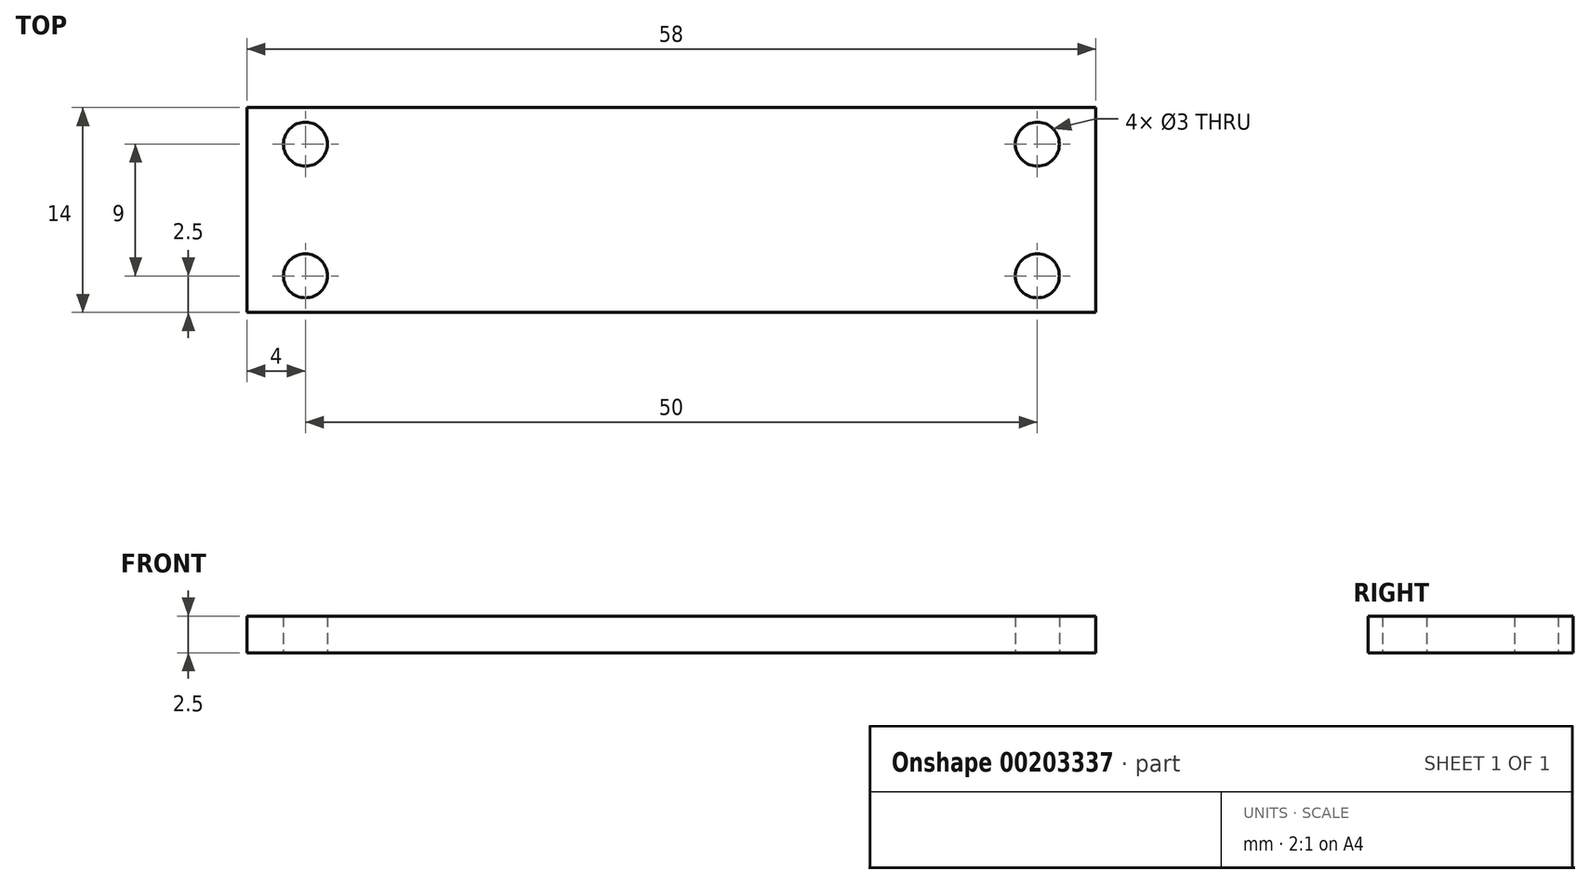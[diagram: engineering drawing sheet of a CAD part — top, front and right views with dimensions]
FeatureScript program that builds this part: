
annotation { "Feature Type Name" : "Feature", "Feature Type Description" : "" }
export const myFeature = defineFeature(function(context is Context, id is Id, definition is map)
    precondition{}
    {
        {
            var Q0;
            Q0=qCreatedBy(makeId("Top.planeOp"),FACE);
            var sketch = newSketch(context, id + "F0", { "sketchPlane" : qUnion([Q0])});
            skLineSegment(sketch, "E0.bottom", {"start": v(-29, 14) * mm, "end": v(29, 14) * mm});
            skLineSegment(sketch, "E0.top", {"start": v(-29, 9) * mm, "end": v(29, 9) * mm});
            skLineSegment(sketch, "E0.left", {"start": v(-29, 14) * mm, "end": v(-29, 9) * mm});
            skLineSegment(sketch, "E0.right", {"start": v(29, 14) * mm, "end": v(29, 9) * mm});
            skLineSegment(sketch, "E1", {"start": v(-29, 11.5) * mm, "end": v(29, 11.5) * mm, "construction": true});
            skCircle(sketch, "E2", {"center": v(-25, 11.5) * mm, "radius": 1.5 * mm});
            skCircle(sketch, "E3", {"center": v(25, 11.5) * mm, "radius": 1.5 * mm});
            skLineSegment(sketch, "E4", {"start": v(0, 14) * mm, "end": v(0, 9) * mm, "construction": true});
            skLineSegment(sketch, "E5.top", {"start": v(-29, 0) * mm, "end": v(29, 0) * mm});
            skLineSegment(sketch, "E5.left", {"start": v(-29, 9) * mm, "end": v(-29, 0) * mm});
            skLineSegment(sketch, "E5.right", {"start": v(29, 9) * mm, "end": v(29, 0) * mm});
            skLineSegment(sketch, "E6", {"start": v(-29, 5) * mm, "end": v(29, 5) * mm, "construction": true});
            skLineSegment(sketch, "E7", {"start": v(-29, 2.5) * mm, "end": v(29, 2.5) * mm, "construction": true});
            skCircle(sketch, "E8", {"center": v(-25, 2.5) * mm, "radius": 1.5 * mm});
            skCircle(sketch, "E9", {"center": v(25, 2.5) * mm, "radius": 1.5 * mm});
            skSolve(sketch);
        }
        {
            var Q0;
            Q0 = qSketchRegion(id + "F0", true);
            extrude(context, id + "F1", {"entities" : qUnion([Q0]), "depth" : 2.5 * mm});
        }
    });
